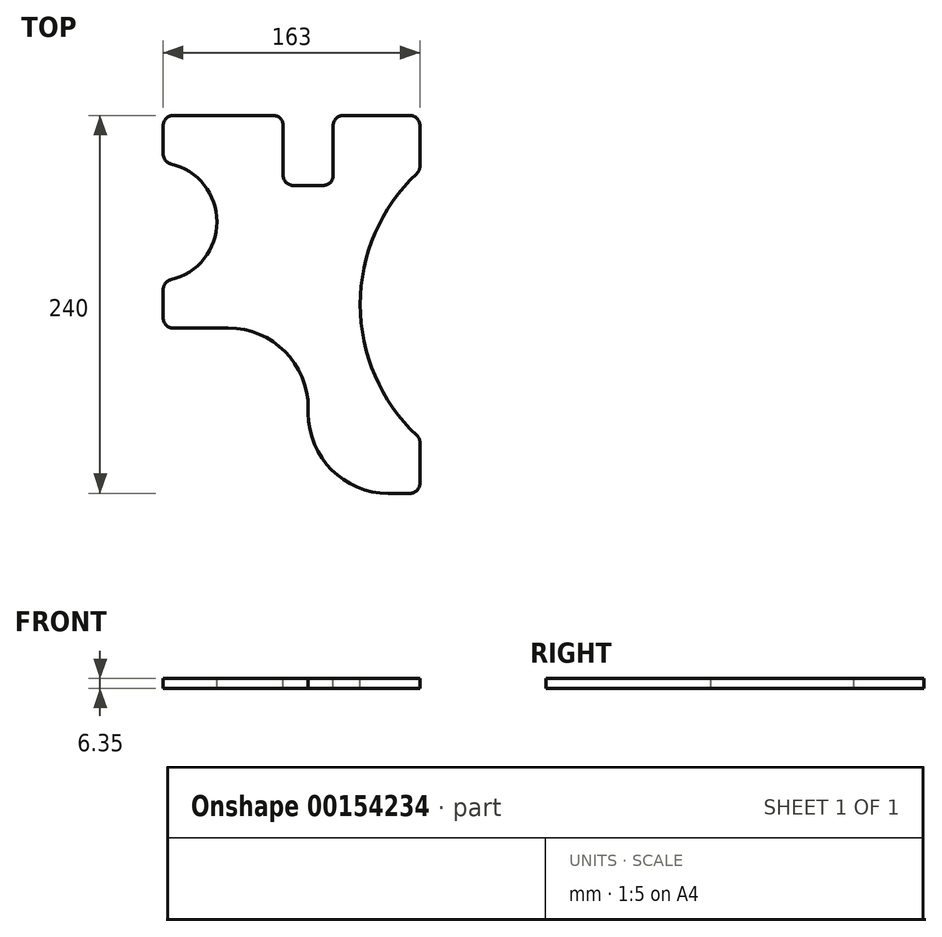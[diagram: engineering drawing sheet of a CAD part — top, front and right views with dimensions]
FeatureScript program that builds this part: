
annotation { "Feature Type Name" : "Feature", "Feature Type Description" : "" }
export const myFeature = defineFeature(function(context is Context, id is Id, definition is map)
    precondition{}
    {
        {
            var Q0;
            Q0=qCreatedBy(makeId("Top.planeOp"),FACE);
            var sketch = newSketch(context, id + "F0", { "sketchPlane" : qUnion([Q0])});
            skLineSegment(sketch, "E0", {"start": v(-92.08, 9.61) * mm, "end": v(-92.08, -8.65) * mm});
            skLineSegment(sketch, "E1", {"start": v(-85.72, -15) * mm, "end": v(-50.8, -15) * mm});
            skLineSegment(sketch, "E2", {"start": v(0, -65.8) * mm, "end": v(0, -69.2) * mm});
            skLineSegment(sketch, "E3", {"start": v(50.8, -120) * mm, "end": v(64.58, -120) * mm});
            skLineSegment(sketch, "E4", {"start": v(70.92, -113.65) * mm, "end": v(70.92, -87.78) * mm});
            skLineSegment(sketch, "E5", {"start": v(70.92, 87.78) * mm, "end": v(70.92, 113.65) * mm});
            skLineSegment(sketch, "E6", {"start": v(64.58, 120) * mm, "end": v(22.22, 120) * mm});
            skLineSegment(sketch, "E7", {"start": v(15.87, 113.65) * mm, "end": v(15.87, 81.9) * mm});
            skLineSegment(sketch, "E8", {"start": v(9.52, 75.55) * mm, "end": v(-9.53, 75.55) * mm});
            skLineSegment(sketch, "E9", {"start": v(-15.88, 81.9) * mm, "end": v(-15.88, 113.65) * mm});
            skLineSegment(sketch, "E10", {"start": v(-22.23, 120) * mm, "end": v(-85.73, 120) * mm});
            skLineSegment(sketch, "E11", {"start": v(-92.08, 113.65) * mm, "end": v(-92.08, 95.39) * mm});
            skArc(sketch, "E12", {"start": v(-87.15, 15.8) * mm, "mid": v(-57.96, 52.5) * mm, "end": v(-87.15, 89.2) * mm});
            skArc(sketch, "E13", {"start": v(68.93, 83.16) * mm, "mid": v(33.04, 0) * mm, "end": v(68.93, -83.16) * mm});
            skPoint(sketch, "E14.visualSharp", {"position": v(0, -15) * mm});
            skArc(sketch, "E14.filletArc", {"start": v(0, -65.8) * mm, "mid": v(-14.88, -29.88) * mm, "end": v(-50.8, -15) * mm});
            skPoint(sketch, "E15.visualSharp", {"position": v(0, -120) * mm});
            skArc(sketch, "E15.filletArc", {"start": v(0, -69.2) * mm, "mid": v(14.88, -105.12) * mm, "end": v(50.8, -120) * mm});
            skPoint(sketch, "E16.visualSharp", {"position": v(-92.08, 120) * mm});
            skArc(sketch, "E16.filletArc", {"start": v(-85.73, 120) * mm, "mid": v(-90.22, 118.14) * mm, "end": v(-92.08, 113.65) * mm});
            skPoint(sketch, "E17.visualSharp", {"position": v(-92.08, 90) * mm});
            skArc(sketch, "E17.filletArc", {"start": v(-92.08, 95.39) * mm, "mid": v(-90.7, 91.44) * mm, "end": v(-87.15, 89.2) * mm});
            skPoint(sketch, "E18.visualSharp", {"position": v(-92.08, 15) * mm});
            skArc(sketch, "E18.filletArc", {"start": v(-87.15, 15.8) * mm, "mid": v(-90.7, 13.56) * mm, "end": v(-92.08, 9.61) * mm});
            skPoint(sketch, "E19.visualSharp", {"position": v(-92.08, -15) * mm});
            skArc(sketch, "E19.filletArc", {"start": v(-92.07, -8.65) * mm, "mid": v(-90.22, -13.14) * mm, "end": v(-85.72, -15) * mm});
            skPoint(sketch, "E20.visualSharp", {"position": v(70.93, -120) * mm});
            skArc(sketch, "E20.filletArc", {"start": v(64.58, -120) * mm, "mid": v(69.07, -118.14) * mm, "end": v(70.92, -113.65) * mm});
            skPoint(sketch, "E21.visualSharp", {"position": v(70.92, -85) * mm});
            skArc(sketch, "E21.filletArc", {"start": v(70.92, -87.78) * mm, "mid": v(70.4, -85.27) * mm, "end": v(68.93, -83.16) * mm});
            skPoint(sketch, "E22.visualSharp", {"position": v(70.92, 85) * mm});
            skArc(sketch, "E22.filletArc", {"start": v(68.93, 83.16) * mm, "mid": v(70.4, 85.27) * mm, "end": v(70.92, 87.78) * mm});
            skPoint(sketch, "E23.visualSharp", {"position": v(70.92, 120) * mm});
            skArc(sketch, "E23.filletArc", {"start": v(70.92, 113.65) * mm, "mid": v(69.07, 118.14) * mm, "end": v(64.58, 120) * mm});
            skPoint(sketch, "E24.visualSharp", {"position": v(15.88, 120) * mm});
            skArc(sketch, "E24.filletArc", {"start": v(22.22, 120) * mm, "mid": v(17.73, 118.14) * mm, "end": v(15.87, 113.65) * mm});
            skPoint(sketch, "E25.visualSharp", {"position": v(15.87, 75.55) * mm});
            skArc(sketch, "E25.filletArc", {"start": v(9.52, 75.55) * mm, "mid": v(14.02, 77.4) * mm, "end": v(15.87, 81.9) * mm});
            skPoint(sketch, "E26.visualSharp", {"position": v(-15.88, 75.55) * mm});
            skArc(sketch, "E26.filletArc", {"start": v(-15.88, 81.9) * mm, "mid": v(-14.02, 77.4) * mm, "end": v(-9.53, 75.55) * mm});
            skPoint(sketch, "E27.visualSharp", {"position": v(-15.88, 120) * mm});
            skArc(sketch, "E27.filletArc", {"start": v(-15.88, 113.65) * mm, "mid": v(-17.73, 118.14) * mm, "end": v(-22.23, 120) * mm});
            skSolve(sketch);
        }
        {
            var Q0;
            Q0 = qSketchRegion(id + "F0", true);
            extrude(context, id + "F1", {"entities" : qUnion([Q0]), "oppositeDirection" : true, "depth" : 6.35 * mm});
        }
    });
